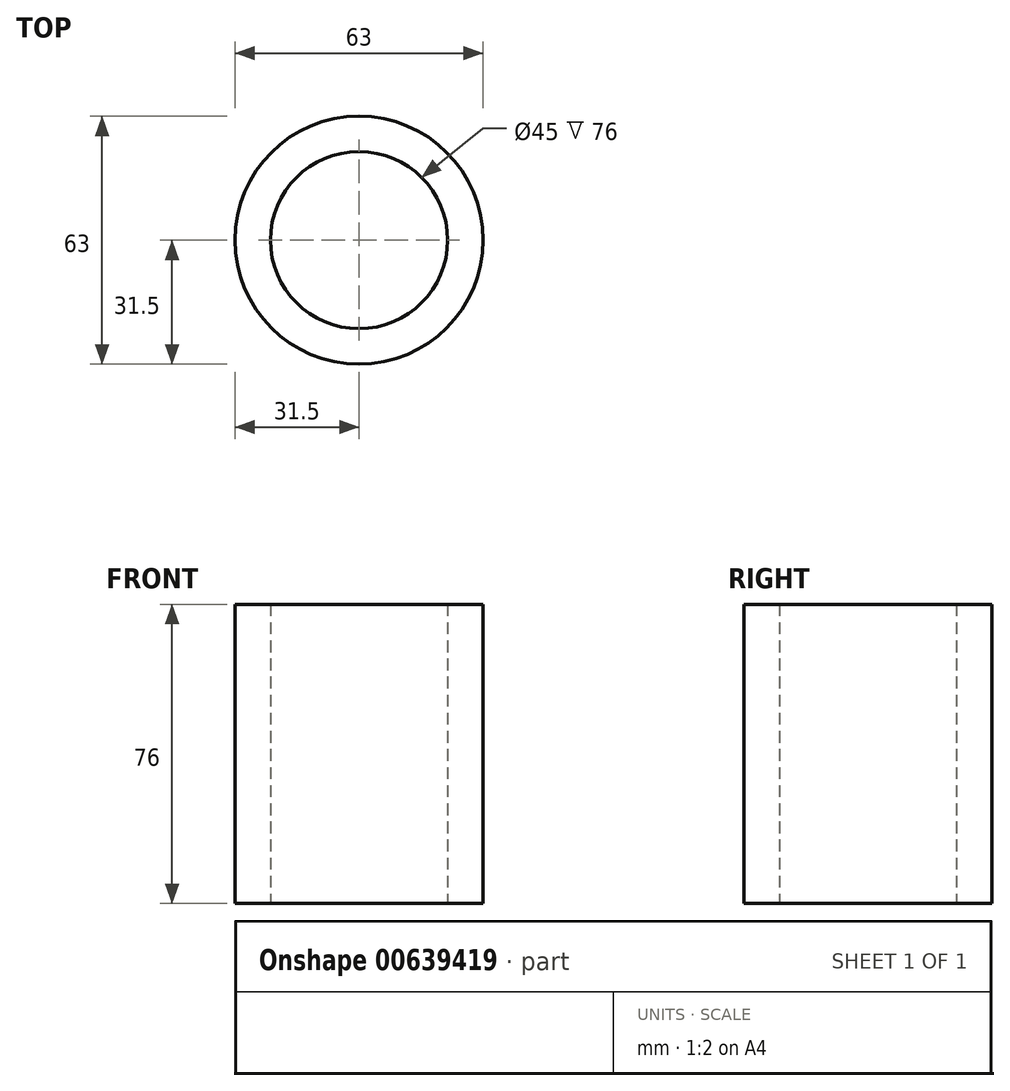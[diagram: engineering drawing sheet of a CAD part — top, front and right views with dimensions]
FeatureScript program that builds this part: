
annotation { "Feature Type Name" : "Feature", "Feature Type Description" : "" }
export const myFeature = defineFeature(function(context is Context, id is Id, definition is map)
    precondition{}
    {
        {
            var Q0;
            Q0=qCreatedBy(makeId("Top.planeOp"),FACE);
            var sketch = newSketch(context, id + "F0", { "sketchPlane" : qUnion([Q0])});
            skCircle(sketch, "E0", {"center": v(0, 0) * mm, "radius": 31.5 * mm});
            skCircle(sketch, "E1", {"center": v(0, 0) * mm, "radius": 22.5 * mm});
            skSolve(sketch);
        }
        {
            var Q0;
            Q0=makeQuery(id+"F0.imprint","IMPRINT",FACE,{"disambiguationData":[TD([[makeQuery(id+"F0.imprint","IMPRINT",EDGE,{"derivedFrom":sQuery(id+"F0.wireOp",EDGE,"E0")}),1.0]])]});
            extrude(context, id + "F1", {"entities" : qUnion([Q0]), "depth" : 76 * mm, "offsetDistance" : 25 * mm});
        }
    });
